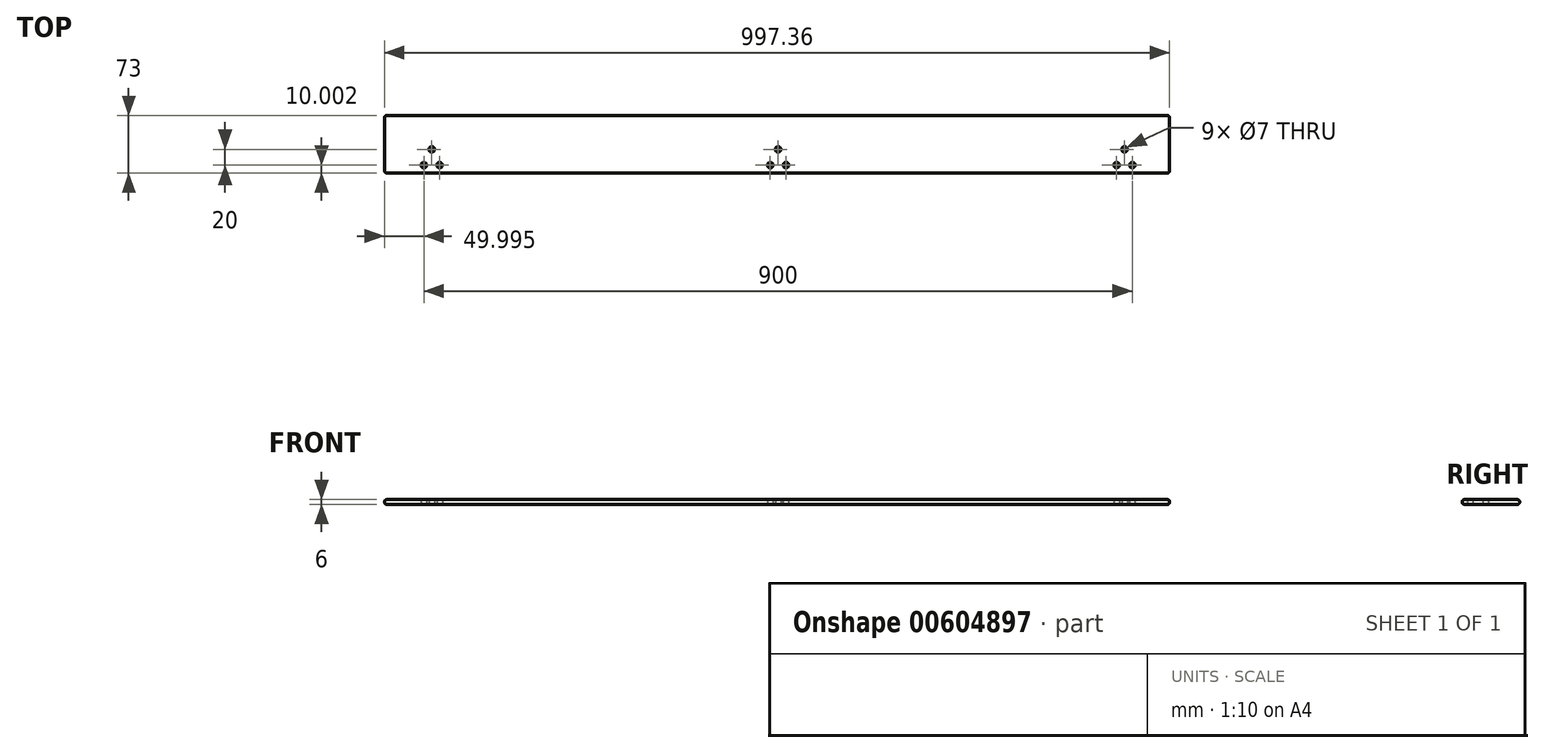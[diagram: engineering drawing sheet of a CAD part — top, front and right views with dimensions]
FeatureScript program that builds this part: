
annotation { "Feature Type Name" : "Feature", "Feature Type Description" : "" }
export const myFeature = defineFeature(function(context is Context, id is Id, definition is map)
    precondition{}
    {
        {
            var Q0;
            Q0=qCreatedBy(makeId("Top.planeOp"),FACE);
            var sketch = newSketch(context, id + "F0", { "sketchPlane" : qUnion([Q0])});
            skLineSegment(sketch, "E0.bottom", {"start": v(-158.18, 34.76) * mm, "end": v(833.18, 34.76) * mm});
            skLineSegment(sketch, "E0.top", {"start": v(-158.18, -38.24) * mm, "end": v(833.18, -38.24) * mm});
            skLineSegment(sketch, "E0.left", {"start": v(-161.18, 31.76) * mm, "end": v(-161.18, -35.24) * mm});
            skLineSegment(sketch, "E0.right", {"start": v(836.18, 31.76) * mm, "end": v(836.18, -35.24) * mm});
            skCircle(sketch, "E1", {"center": v(788.82, -28.24) * mm, "radius": 3.5 * mm});
            skCircle(sketch, "E2", {"center": v(778.82, -8.24) * mm, "radius": 3.5 * mm});
            skCircle(sketch, "E3", {"center": v(768.82, -28.24) * mm, "radius": 3.5 * mm});
            skCircle(sketch, "E4", {"center": v(348.82, -28.24) * mm, "radius": 3.5 * mm});
            skCircle(sketch, "E5", {"center": v(338.82, -8.24) * mm, "radius": 3.5 * mm});
            skCircle(sketch, "E6", {"center": v(328.82, -28.24) * mm, "radius": 3.5 * mm});
            skCircle(sketch, "E7", {"center": v(-111.18, -28.24) * mm, "radius": 3.5 * mm});
            skCircle(sketch, "E8", {"center": v(-91.18, -28.24) * mm, "radius": 3.5 * mm});
            skCircle(sketch, "E9", {"center": v(-101.18, -8.24) * mm, "radius": 3.5 * mm});
            skPoint(sketch, "E10.visualSharp", {"position": v(-161.18, 34.76) * mm});
            skArc(sketch, "E10.filletArc", {"start": v(-158.18, 34.76) * mm, "mid": v(-160.3, 33.88) * mm, "end": v(-161.18, 31.76) * mm});
            skPoint(sketch, "E11.visualSharp", {"position": v(-161.18, -38.24) * mm});
            skArc(sketch, "E11.filletArc", {"start": v(-161.18, -35.24) * mm, "mid": v(-160.3, -37.36) * mm, "end": v(-158.18, -38.24) * mm});
            skPoint(sketch, "E12.visualSharp", {"position": v(836.18, 34.76) * mm});
            skPoint(sketch, "E13.visualSharp", {"position": v(836.18, -38.24) * mm});
            skArc(sketch, "E13.filletArc", {"start": v(833.18, -38.24) * mm, "mid": v(835.3, -37.36) * mm, "end": v(836.18, -35.24) * mm});
            skArc(sketch, "E14.filletArc", {"start": v(836.18, 31.76) * mm, "mid": v(835.3, 33.88) * mm, "end": v(833.18, 34.76) * mm});
            skSolve(sketch);
        }
        {
            var Q0;
            Q0 = qSketchRegion(id + "F0", true);
            extrude(context, id + "F1", {"entities" : qUnion([Q0]), "depth" : 6 * mm, "offsetDistance" : 25 * mm});
        }
        {
            var Q0;
            Q0=makeQuery(id+"F1.opExtrude","SWEPT_FACE",FACE,{"disambiguationData":[OSD([sQuery(id+"F0.wireOp",EDGE,"E0.right")])]});
            fillet(context, id + "F2", {"entities" : qUnion([Q0]), "radius" : 3 * mm, "tangentPropagation" : true, "allowEdgeOverflow" : false});
        }
    });
